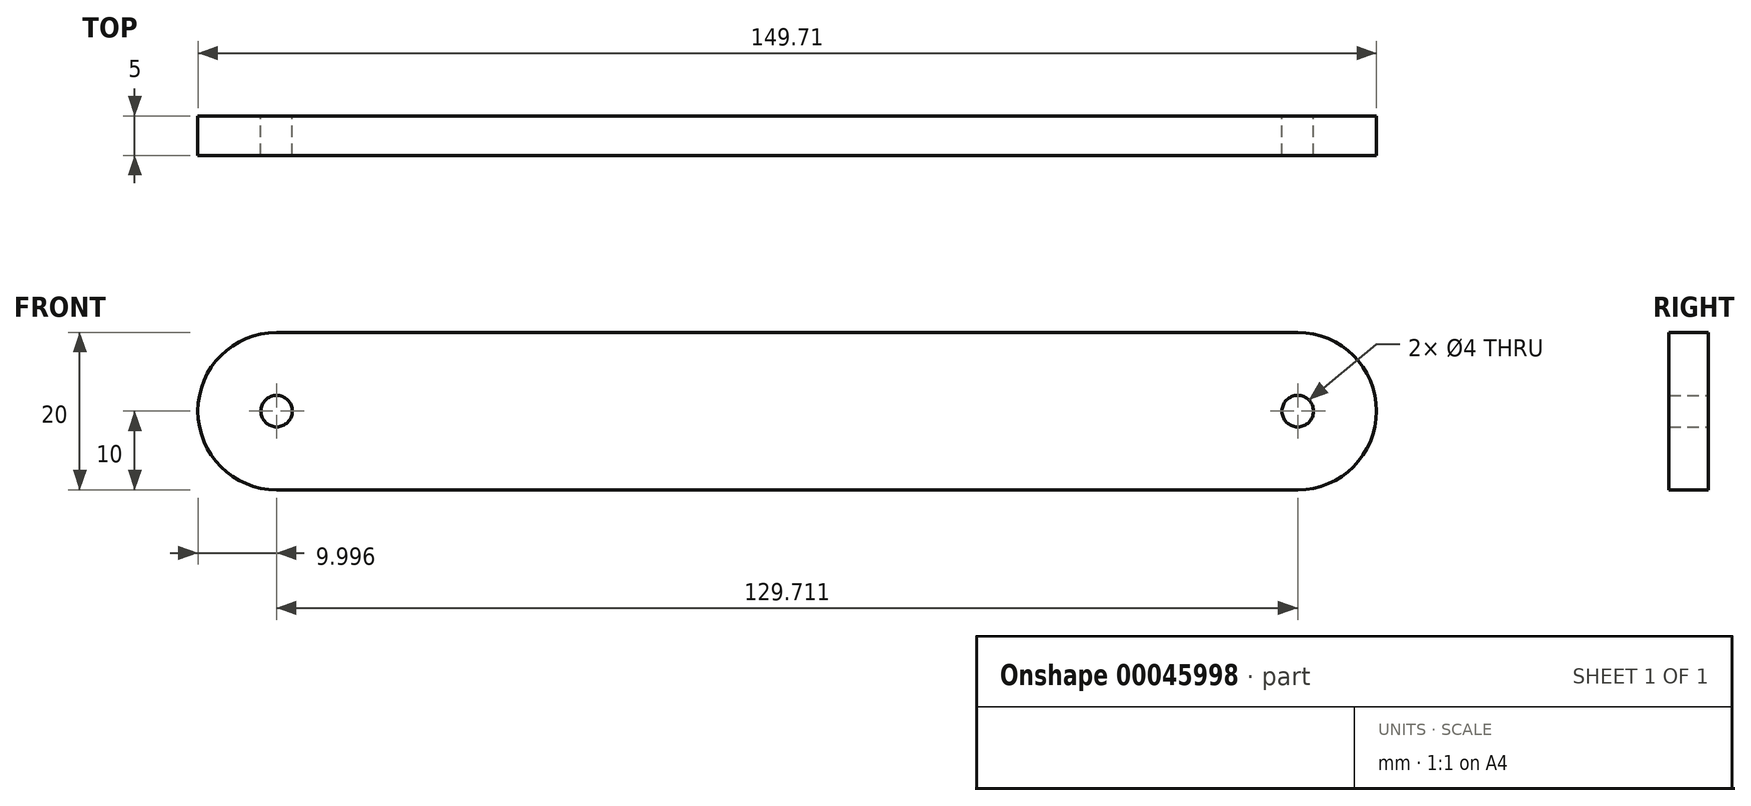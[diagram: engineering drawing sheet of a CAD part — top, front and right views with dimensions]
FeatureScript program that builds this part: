
annotation { "Feature Type Name" : "Feature", "Feature Type Description" : "" }
export const myFeature = defineFeature(function(context is Context, id is Id, definition is map)
    precondition{}
    {
        {
            var Q0;
            Q0=qCreatedBy(makeId("Front.planeOp"),FACE);
            var sketch = newSketch(context, id + "F0", { "sketchPlane" : qUnion([Q0])});
            skPoint(sketch, "E0", {"position": v(-71.37, 0) * mm});
            skPoint(sketch, "E1", {"position": v(58.34, 0) * mm});
            skCircle(sketch, "E2", {"center": v(-71.37, 0) * mm, "radius": 2 * mm});
            skCircle(sketch, "E3", {"center": v(58.34, 0) * mm, "radius": 2 * mm});
            skArc(sketch, "E4", {"start": v(-71.37, 10) * mm, "mid": v(-81.37, 0) * mm, "end": v(-71.37, -10) * mm});
            skArc(sketch, "E5", {"start": v(58.34, 10) * mm, "mid": v(68.34, 0) * mm, "end": v(58.34, -10) * mm});
            skLineSegment(sketch, "E6", {"start": v(-71.37, 10) * mm, "end": v(58.34, 10) * mm});
            skLineSegment(sketch, "E7", {"start": v(58.34, -10) * mm, "end": v(-71.37, -10) * mm});
            skLineSegment(sketch, "E8", {"start": v(-71.37, 0) * mm, "end": v(58.34, 0) * mm, "construction": true});
            skSolve(sketch);
        }
        {
            var Q0;
            Q0 = qSketchRegion(id + "F0", true);
            extrude(context, id + "F1", {"entities" : qUnion([Q0]), "depth" : 5 * mm});
        }
    });
